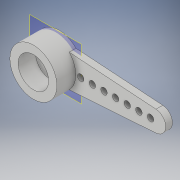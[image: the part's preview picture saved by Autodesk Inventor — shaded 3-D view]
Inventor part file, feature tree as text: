
AUTODESK INVENTOR PART (.ipt)
format: ipt  version: 2017 (Build 210142000, 142)  size: 158,208 bytes
history: native  units: in
note: dims shown in document units (in); Inventor stores cm internally (conversion verified against a paired STEP export)
features: extrude x6, sketch x6, plane x1, pattern_linear x1
ambient origin geometry x8: Origin, YZ Plane, XZ Plane, XY Plane, X Axis, Y Axis, Z Axis, Center Point
bodies: Solid1 (feature_tree)
feature tree (14):
  extrude  "Extrusion1"  Depth=0.159in TaperAngle=0.0deg
  extrude  "Extrusion2"  Depth=0.108in TaperAngle=0.0deg
  extrude  "Extrusion3"  Depth=0.042in TaperAngle=0.0deg
  extrude  "Extrusion4"  Depth=0.042in TaperAngle=0.0deg
  plane  "Work Plane1"
  extrude  "Extrusion5"  Depth=0.16in
  extrude  "Extrusion6"  Depth=0.042in TaperAngle=0.0deg
  pattern_linear  "Rectangular Pattern1"  Spacing1=0.042in  [1 undecoded]
  sketch  "Sketch1"  dims[d0=0.291in d1=0.159in d2=0.0in]
  sketch  "Sketch2"  dims[d3=0.051in d4=0.108in d5=0.0in]
  sketch  "Sketch3"  dims[d6=0.06in d7=0.042in d8=0.0in]
  sketch  "Sketch4"  dims[d9=0.114in d10=0.042in d11=0.0in]
  sketch  "Sketch5"  dims[d12=0.202in d13=0.16in]
  sketch  "Sketch6"  dims[d15=0.638in d16=0.042in d17=0.0in d24=0.042in d25=0.0in d26=0.7874in d28=360.0deg d35=0.128in d36=0.071in d37=0.04in d38=2.7559in d40=0.072in]
note: 1 required parameter value undecoded (feature->parameter linkage not recoverable at this tier; creation-order binding heuristic only, values carry confidence <= 0.55)
